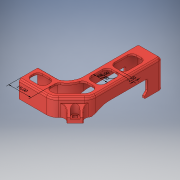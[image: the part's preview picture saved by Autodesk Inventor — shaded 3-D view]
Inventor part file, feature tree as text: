
AUTODESK INVENTOR PART (.ipt)
format: ipt  version: 2019.4 (Build 234330000, 330)  size: 1,062,400 bytes
history: native  units: in
note: dims shown in document units (in); Inventor stores cm internally (conversion verified against a paired STEP export)
features: other x6, extrude x3, sketch x3, projected_geometry x1
ambient origin geometry x8: Origin, YZ Plane, XZ Plane, XY Plane, X Axis, Y Axis, Z Axis, Center Point
bodies: Solid1 (feature_tree)
feature tree (13):
  other  "Annotations"
  extrude  "Extrusion1"  Depth=0.0591in
  extrude  "Extrusion2"  Depth=0.6385in
  extrude  "Extrusion3"  Depth=0.3937in
  sketch  "Sketch1"  dims[d3=0.6437in d4=0.0in d6=0.0591in]
  sketch  "Sketch2"  dims[d7=0.689in d8=0.0in d19=0.6385in]
  sketch  "Sketch3"  dims[d20=0.0984in d21=0.3937in d22=0.1224in d23=0.0984in d24=0.1575in d25=0.748in d26=0.0in d10=0.748in d11=1.198in d12=0.1575in d13=0.2117in d14=0.1423in d15=0.0984in d16=0.236in d17=0.2724in d18=0.4724in d9=0.1536in]
  other  "[a]_xz_cable_cover"
  projected_geometry  "Project Cut Edges1"
  other  "Linear Dimension 1"
  other  "Radial Dimension 1"
  other  "Linear Dimension 2"
  other  "Linear Dimension 3"
